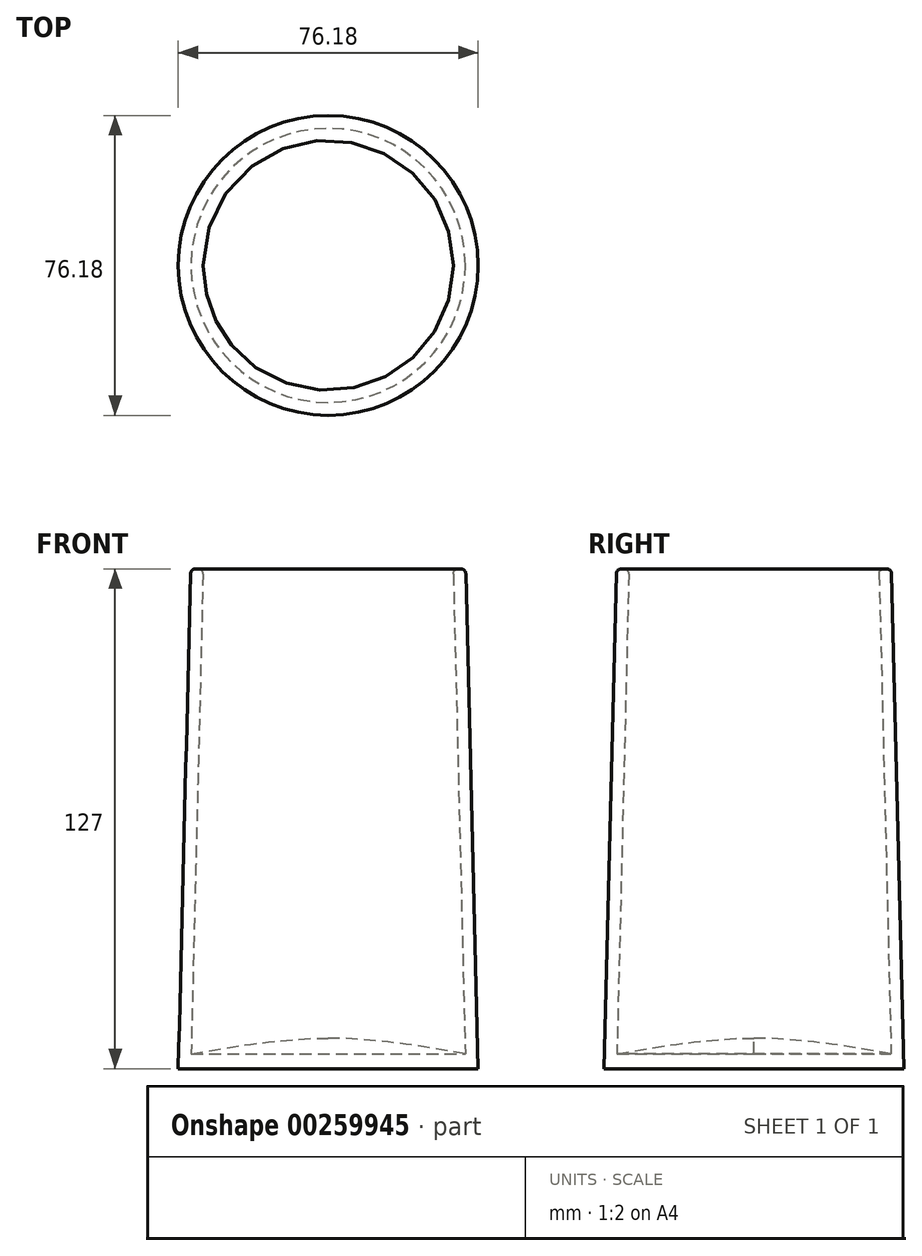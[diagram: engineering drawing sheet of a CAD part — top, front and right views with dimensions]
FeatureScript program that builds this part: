
annotation { "Feature Type Name" : "Feature", "Feature Type Description" : "" }
export const myFeature = defineFeature(function(context is Context, id is Id, definition is map)
    precondition{}
    {
        {
            var Q0;
            Q0=qCreatedBy(makeId("Top.planeOp"),FACE);
            var sketch = newSketch(context, id + "F0", { "sketchPlane" : qUnion([Q0])});
            skCircle(sketch, "E0", {"center": v(0, 0) * mm, "radius": 38.1 * mm});
            skCircle(sketch, "E1", {"center": v(0, 0) * mm, "radius": 34.93 * mm});
            skSolve(sketch);
        }
        {
            var Q0;
            Q0=qCreatedBy(makeId("Front.planeOp"),FACE);
            var sketch = newSketch(context, id + "F1", { "sketchPlane" : qUnion([Q0])});
            skLineSegment(sketch, "E2", {"start": v(0, 0) * mm, "end": v(0, 127) * mm, "construction": true});
            skLineSegment(sketch, "E3", {"start": v(-34.93, 127) * mm, "end": v(34.93, 127) * mm, "construction": true});
            skLineSegment(sketch, "E4", {"start": v(-38.09, 0) * mm, "end": v(-34.93, 127) * mm});
            skLineSegment(sketch, "E5", {"start": v(-34.93, 0) * mm, "end": v(-31.76, 127) * mm});
            skLineSegment(sketch, "E6", {"start": v(-31.76, 127) * mm, "end": v(-34.93, 127) * mm});
            skLineSegment(sketch, "E7", {"start": v(-38.09, 0) * mm, "end": v(-34.93, 0) * mm});
            skLineSegment(sketch, "E8", {"start": v(0, 0) * mm, "end": v(-34.93, 0) * mm});
            skLineSegment(sketch, "E9", {"start": v(-34.93, 0) * mm, "end": v(-34.83, 3.8) * mm});
            skLineSegment(sketch, "E10", {"start": v(0, 0) * mm, "end": v(34.93, 0) * mm, "construction": true});
            skLineSegment(sketch, "E11", {"start": v(34.93, 0) * mm, "end": v(34.83, 3.8) * mm, "construction": true});
            skFitSpline(sketch, "E12", {"points": [v(-34.83, 3.8) * mm, v(0, 7.74) * mm, v(34.83, 3.8) * mm], "startDerivative": vector(69.66, 11.8) * mm, "endDerivative": vector(69.66, -11.83) * mm});
            skLineSegment(sketch, "E13", {"start": v(0, 7.74) * mm, "end": v(0, 0) * mm});
            skSolve(sketch);
        }
        {
            var Q0;
            Q0=makeQuery(id+"F1.imprint","IMPRINT",FACE,{"disambiguationData":[TD([[makeQuery(id+"F1.imprint","IMPRINT",EDGE,{"derivedFrom":sQuery(id+"F1.wireOp",EDGE,"E4")}),-1.0]])]});
            var Q1;
            Q1=makeQuery(id+"F1.imprint","IMPRINT",FACE,{"disambiguationData":[TD([[makeQuery(id+"F1.imprint","IMPRINT",EDGE,{"derivedFrom":sQuery(id+"F1.wireOp",EDGE,"E8")}),-1.0]])]});
            var Q2;
            Q2=sQuery(id+"F1.wireOp",EDGE,"E2");
            revolve(context, id + "F2", {"entities" : qUnion([Q0, Q1]), "axis" : qUnion([Q2]), "revolveType" : RevolveType.FULL});
        }
        {
            var Q0;
            Q0=makeQuery(id+"F2.opRevolve","SWEPT_EDGE",EDGE,{"disambiguationData":[OSD([sQuery(id+"F1.wireOp",EDGE,"E4"),sQuery(id+"F1.wireOp",EDGE,"E6")])]});
            var Q1;
            Q1=makeQuery(id+"F2.opRevolve","SWEPT_EDGE",EDGE,{"disambiguationData":[OSD([sQuery(id+"F1.wireOp",EDGE,"E5"),sQuery(id+"F1.wireOp",EDGE,"E6")])]});
            fillet(context, id + "F3", {"entities" : qUnion([Q0, Q1]), "radius" : 1.27 * mm, "tangentPropagation" : true, "allowEdgeOverflow" : false});
        }
    });
